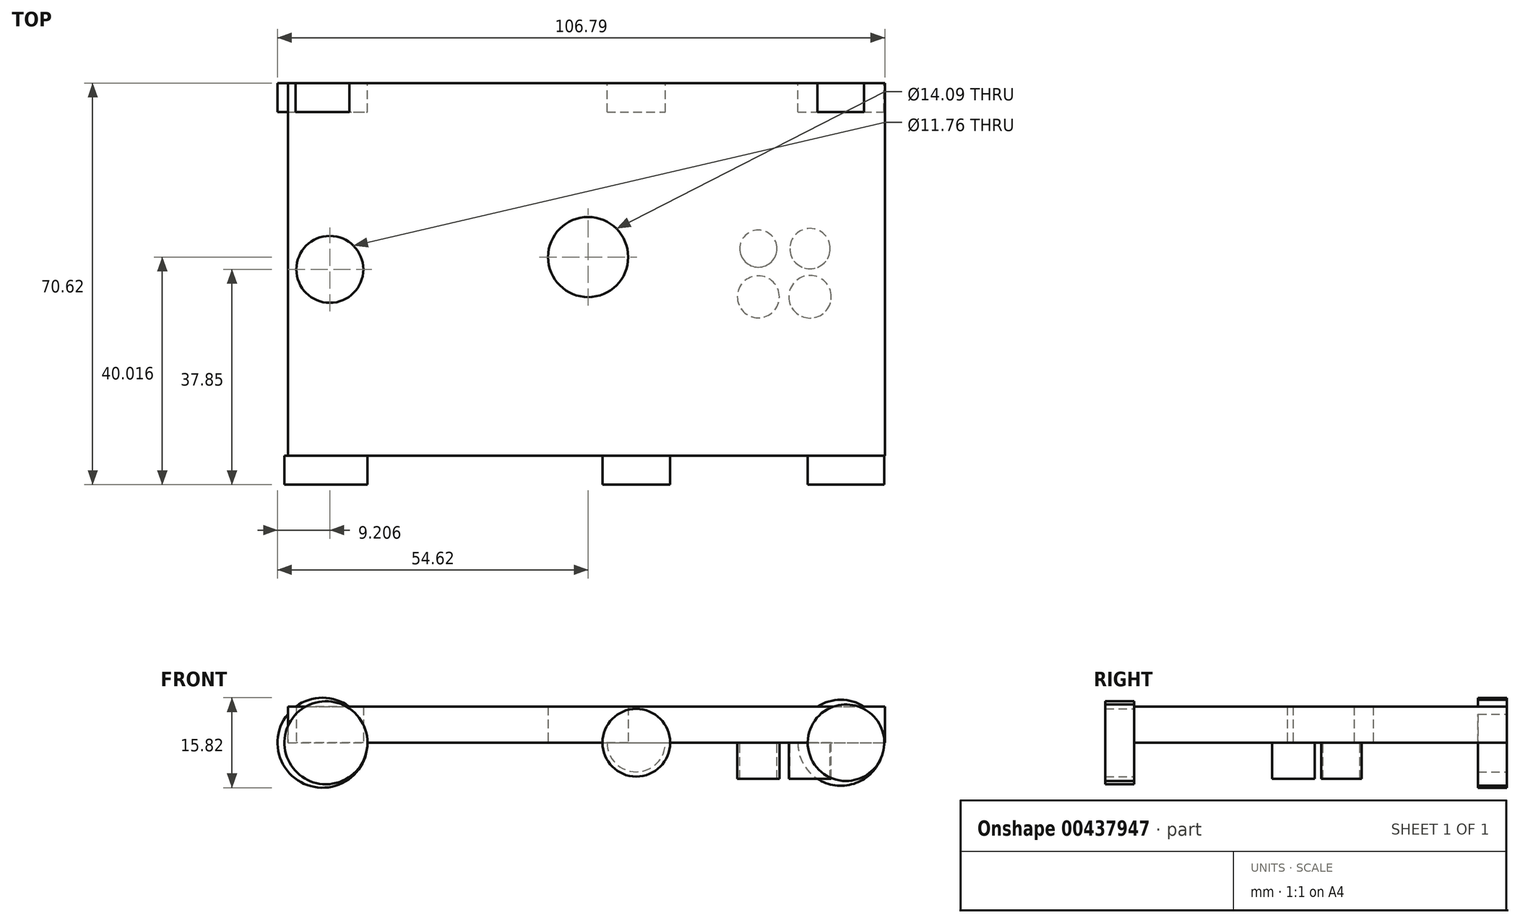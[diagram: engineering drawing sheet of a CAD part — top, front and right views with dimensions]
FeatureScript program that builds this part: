
annotation { "Feature Type Name" : "Feature", "Feature Type Description" : "" }
export const myFeature = defineFeature(function(context is Context, id is Id, definition is map)
    precondition{}
    {
        {
            var Q0;
            Q0=qCreatedBy(makeId("Top.planeOp"),FACE);
            var sketch = newSketch(context, id + "F0", { "sketchPlane" : qUnion([Q0])});
            skLineSegment(sketch, "E0.right", {"start": v(-61.26, -32.77) * mm, "end": v(-61.26, 32.77) * mm});
            skPoint(sketch, "E0.middle", {"position": v(0, 0) * mm});
            skCircle(sketch, "E1", {"center": v(-8.46, 2.17) * mm, "radius": 7.05 * mm});
            skPoint(sketch, "E1.first.point", {"position": v(-12.2, -3.81) * mm});
            skPoint(sketch, "E1.second.point", {"position": v(-5.8, 8.69) * mm});
            skPoint(sketch, "E1.third.point", {"position": v(-13.72, 6.86) * mm});
            skLineSegment(sketch, "E2.bottom", {"start": v(0, 32.77) * mm, "end": v(43.7, 32.77) * mm});
            skLineSegment(sketch, "E2.top", {"start": v(0, -32.77) * mm, "end": v(43.7, -32.77) * mm});
            skLineSegment(sketch, "E2.left", {"start": v(0, 32.77) * mm, "end": v(0, -32.77) * mm});
            skLineSegment(sketch, "E2.right", {"start": v(43.7, 32.77) * mm, "end": v(43.7, -32.77) * mm});
            skLineSegment(sketch, "E3", {"start": v(-61.26, 32.77) * mm, "end": v(0, 32.77) * mm});
            skLineSegment(sketch, "E4", {"start": v(43.7, 32.77) * mm, "end": v(73.74, 27.54) * mm});
            skLineSegment(sketch, "E5", {"start": v(-61.26, -32.77) * mm, "end": v(0, -32.77) * mm});
            skLineSegment(sketch, "E6", {"start": v(43.7, -32.77) * mm, "end": v(73.22, -25.13) * mm});
            skCircle(sketch, "E7", {"center": v(-53.87, 0) * mm, "radius": 5.88 * mm});
            skSolve(sketch);
        }
        {
            var Q0;
            Q0=sQuery(id+"F0.wireOp",EDGE,"E0.right");
            var Q1;
            Q1=sQuery(id+"F0.wireOp",EDGE,"E0.top");
            var Q2;
            Q2=sQuery(id+"F0.wireOp",EDGE,"E0.left");
            var Q3;
            Q3=sQuery(id+"F0.wireOp",EDGE,"E0.bottom");
            extrude(context, id + "F1", {"bodyType" : ToolBodyType.SURFACE, "surfaceEntities" : qUnion([Q0, Q1, Q2, Q3]), "depth" : 12.7 * mm});
        }
        {
            var Q0;
            Q0=sQuery(id+"F0.wireOp",EDGE,"E1");
            extrude(context, id + "F2", {"bodyType" : ToolBodyType.SURFACE, "surfaceEntities" : qUnion([Q0]), "depth" : 38.1 * mm});
        }
        {
            var Q0;
            Q0=makeQuery(id+"F0.imprint","IMPRINT",FACE,{"disambiguationData":[TD([[makeQuery(id+"F0.imprint","IMPRINT",EDGE,{"derivedFrom":sQuery(id+"F0.wireOp",EDGE,"E2.bottom")}),-1.0]])]});
            var Q1;
            Q1=sQuery(id+"F0.wireOp",EDGE,"E2.right");
            var Q2;
            Q2=sQuery(id+"F0.wireOp",EDGE,"E2.bottom");
            var Q3;
            Q3=sQuery(id+"F0.wireOp",EDGE,"E2.left");
            var Q4;
            Q4=sQuery(id+"F0.wireOp",EDGE,"E2.top");
            extrude(context, id + "F3", {"entities" : qUnion([Q0]), "bodyType" : ToolBodyType.SURFACE, "surfaceEntities" : qUnion([Q1, Q2, Q3, Q4]), "depth" : 25.4 * mm});
        }
        {
            var Q0;
            Q0=sQuery(id+"F0.wireOp",EDGE,"E3");
            var Q1;
            Q1=sQuery(id+"F0.wireOp",EDGE,"E4");
            var Q2;
            Q2=sQuery(id+"F0.wireOp",EDGE,"E6");
            var Q3;
            Q3=sQuery(id+"F0.wireOp",EDGE,"E5");
            extrude(context, id + "F4", {"bodyType" : ToolBodyType.SURFACE, "surfaceEntities" : qUnion([Q0, Q1, Q2, Q3]), "depth" : 12.7 * mm});
        }
        {
            var Q0;
            Q0=qCreatedBy(makeId("Top.planeOp"),FACE);
            var sketch = newSketch(context, id + "F5", { "sketchPlane" : qUnion([Q0])});
            skCircle(sketch, "E8", {"center": v(-53.64, 0) * mm, "radius": 4.45 * mm});
            skSolve(sketch);
        }
        {
            var Q0;
            Q0 = qSketchRegion(id + "F5", true);
            var Q1;
            Q1=sQuery(id+"F5.wireOp",EDGE,"E8");
            extrude(context, id + "F6", {"entities" : qUnion([Q0]), "bodyType" : ToolBodyType.SURFACE, "surfaceEntities" : qUnion([Q1]), "depth" : 19.05 * mm});
        }
        {
            var Q0;
            Q0 = qSketchRegion(id + "F0", true);
            extrude(context, id + "F7", {"entities" : qUnion([Q0]), "depth" : 6.35 * mm});
        }
        {
            var Q0;
            Q0=makeQuery(id+"F4.opExtrude","SWEPT_FACE",FACE,{"disambiguationData":[OSD([sQuery(id+"F0.wireOp",EDGE,"E5")])]});
            var sketch = newSketch(context, id + "F8", { "sketchPlane" : qUnion([Q0])});
            skCircle(sketch, "E9", {"center": v(-54.56, 0) * mm, "radius": 7.3 * mm});
            skCircle(sketch, "E10", {"center": v(0, 0) * mm, "radius": 5.95 * mm});
            skCircle(sketch, "E11", {"center": v(36.88, 0) * mm, "radius": 6.73 * mm});
            skSolve(sketch);
        }
        {
            var Q0;
            Q0 = qSketchRegion(id + "F8", true);
            extrude(context, id + "F9", {"entities" : qUnion([Q0]), "operationType" : NewBodyOperationType.ADD, "depth" : 5.08 * mm});
        }
        {
            var Q0;
            Q0=makeQuery(id+"F4.opExtrude","SWEPT_FACE",FACE,{"disambiguationData":[OSD([sQuery(id+"F0.wireOp",EDGE,"E3")])]});
            var sketch = newSketch(context, id + "F10", { "sketchPlane" : qUnion([Q0])});
            skCircle(sketch, "E12", {"center": v(0, 0) * mm, "radius": 5.12 * mm});
            skCircle(sketch, "E13", {"center": v(-55.17, 0) * mm, "radius": 7.9 * mm});
            skCircle(sketch, "E14", {"center": v(35.97, 0) * mm, "radius": 7.57 * mm});
            skSolve(sketch);
        }
        {
            var Q0;
            Q0 = qSketchRegion(id + "F10", true);
            extrude(context, id + "F11", {"entities" : qUnion([Q0]), "operationType" : NewBodyOperationType.ADD, "depth" : 5.08 * mm});
        }
        {
            var Q0;
            Q0=makeQuery(id+"F7.opExtrude","CAP_FACE",FACE,{"disambiguationData":[OSD([sQuery(id+"F0.wireOp",EDGE,"E0.right"),sQuery(id+"F0.wireOp",EDGE,"E1"),sQuery(id+"F0.wireOp",EDGE,"E2.bottom"),sQuery(id+"F0.wireOp",EDGE,"E2.top"),sQuery(id+"F0.wireOp",EDGE,"E2.right"),sQuery(id+"F0.wireOp",EDGE,"E3"),sQuery(id+"F0.wireOp",EDGE,"E5"),sQuery(id+"F0.wireOp",EDGE,"E7")])],"isStart":true});
            var sketch = newSketch(context, id + "F12", { "sketchPlane" : qUnion([Q0])});
            skCircle(sketch, "E15", {"center": v(30.56, 4.82) * mm, "radius": 3.74 * mm});
            skCircle(sketch, "E16", {"center": v(21.47, 4.82) * mm, "radius": 3.7 * mm});
            skCircle(sketch, "E17", {"center": v(30.56, -3.66) * mm, "radius": 3.54 * mm});
            skCircle(sketch, "E18", {"center": v(21.47, -3.66) * mm, "radius": 3.26 * mm});
            skSolve(sketch);
        }
        {
            var Q0;
            Q0=makeQuery(id+"F12.imprint","IMPRINT",FACE,{"disambiguationData":[TD([[makeQuery(id+"F12.imprint","IMPRINT",EDGE,{"derivedFrom":sQuery(id+"F12.wireOp",EDGE,"E15")}),1.0]])]});
            var Q1;
            Q1=makeQuery(id+"F12.imprint","IMPRINT",FACE,{"disambiguationData":[TD([[makeQuery(id+"F12.imprint","IMPRINT",EDGE,{"derivedFrom":sQuery(id+"F12.wireOp",EDGE,"E17")}),1.0]])]});
            var Q2;
            Q2=makeQuery(id+"F12.imprint","IMPRINT",FACE,{"disambiguationData":[TD([[makeQuery(id+"F12.imprint","IMPRINT",EDGE,{"derivedFrom":sQuery(id+"F12.wireOp",EDGE,"E18")}),1.0]])]});
            var Q3;
            Q3=makeQuery(id+"F12.imprint","IMPRINT",FACE,{"disambiguationData":[TD([[makeQuery(id+"F12.imprint","IMPRINT",EDGE,{"derivedFrom":sQuery(id+"F12.wireOp",EDGE,"E16")}),1.0]])]});
            extrude(context, id + "F13", {"entities" : qUnion([Q0, Q1, Q2, Q3]), "operationType" : NewBodyOperationType.ADD, "depth" : 6.35 * mm});
        }
    });
